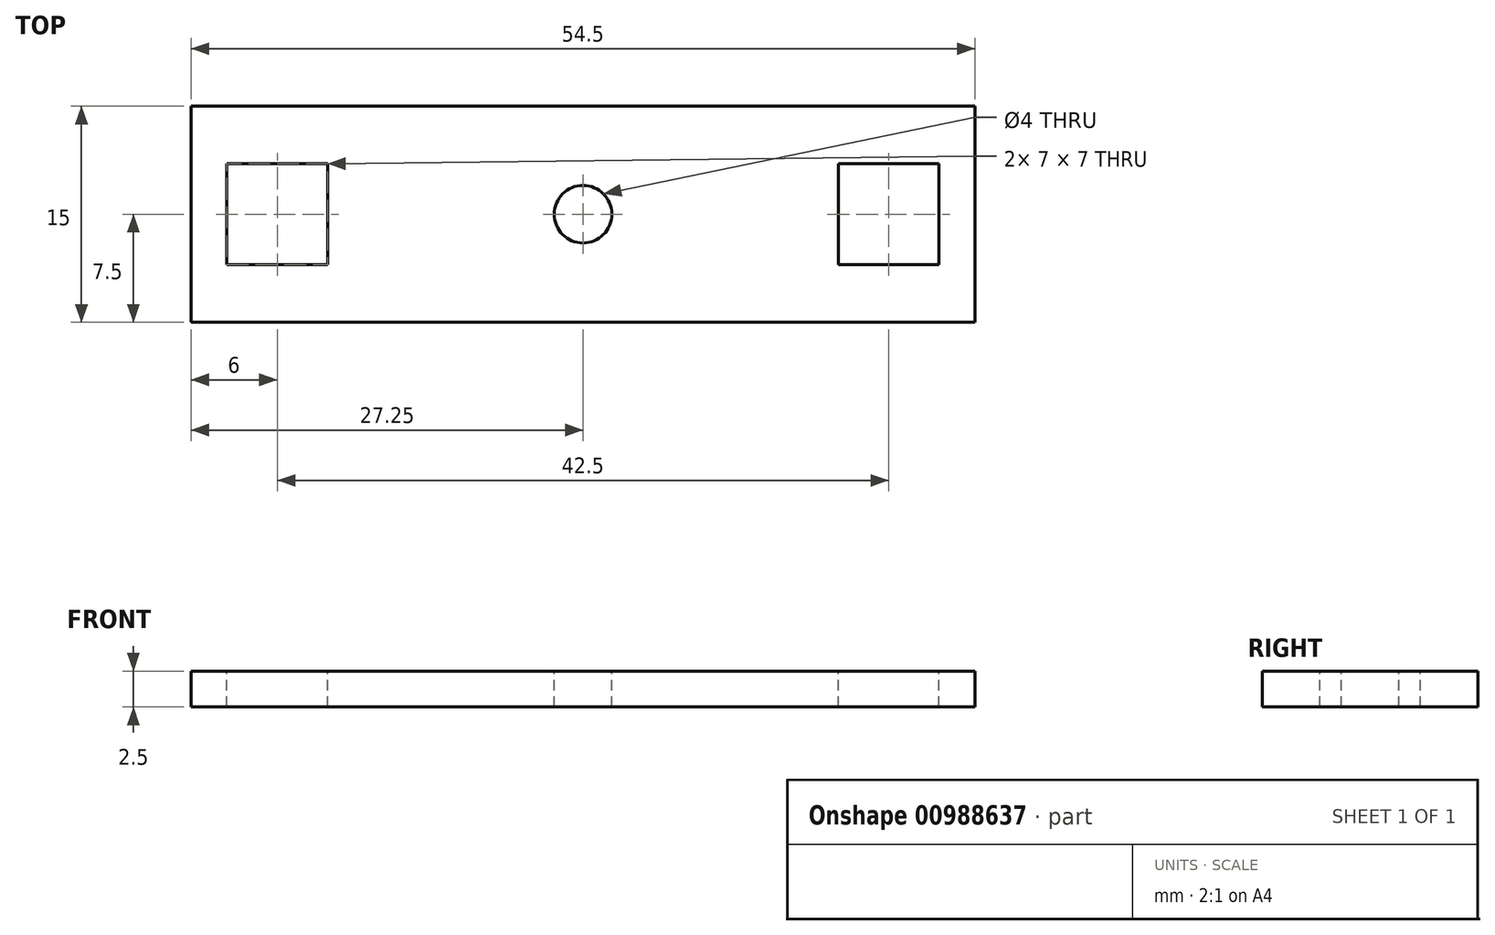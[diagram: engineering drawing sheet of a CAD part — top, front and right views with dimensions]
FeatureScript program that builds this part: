
annotation { "Feature Type Name" : "Feature", "Feature Type Description" : "" }
export const myFeature = defineFeature(function(context is Context, id is Id, definition is map)
    precondition{}
    {
        {
            var Q0;
            Q0=qCreatedBy(makeId("Top.planeOp"),FACE);
            var sketch = newSketch(context, id + "F0", { "sketchPlane" : qUnion([Q0])});
            skLineSegment(sketch, "E0.bottom", {"start": v(27.25, 7.5) * mm, "end": v(-27.25, 7.5) * mm});
            skLineSegment(sketch, "E0.top", {"start": v(27.25, -7.5) * mm, "end": v(-27.25, -7.5) * mm});
            skLineSegment(sketch, "E0.left", {"start": v(27.25, 7.5) * mm, "end": v(27.25, -7.5) * mm});
            skLineSegment(sketch, "E0.right", {"start": v(-27.25, 7.5) * mm, "end": v(-27.25, -7.5) * mm});
            skPoint(sketch, "E0.middle", {"position": v(0, 0) * mm});
            skSolve(sketch);
        }
        {
            var Q0;
            Q0=makeQuery(id+"F0.imprint","IMPRINT",FACE,{"disambiguationData":[TD([[makeQuery(id+"F0.imprint","IMPRINT",EDGE,{"derivedFrom":sQuery(id+"F0.wireOp",EDGE,"E0.bottom")}),1.0]])]});
            extrude(context, id + "F1", {"entities" : qUnion([Q0]), "depth" : 2.5 * mm, "offsetDistance" : 25 * mm});
        }
        {
            var Q0;
            Q0=makeQuery(id+"F1.opExtrude","CAP_FACE",FACE,{"disambiguationData":[OSD([sQuery(id+"F0.wireOp",EDGE,"E0.bottom"),sQuery(id+"F0.wireOp",EDGE,"E0.top"),sQuery(id+"F0.wireOp",EDGE,"E0.left"),sQuery(id+"F0.wireOp",EDGE,"E0.right")])],"isStart":false});
            var sketch = newSketch(context, id + "F2", { "sketchPlane" : qUnion([Q0])});
            skPoint(sketch, "E1", {"position": v(0, 0) * mm});
            skSolve(sketch);
        }
        {
            var Q0;
            Q0=sQuery(id+"F2.wireOp",VERTEX,"E1");
            var Q1;
            Q1=makeQuery(id+"F1.opExtrude","SWEPT_BODY",BODY,{"disambiguationData":[OSD([sQuery(id+"F0.wireOp",EDGE,"E0.bottom"),sQuery(id+"F0.wireOp",EDGE,"E0.top"),sQuery(id+"F0.wireOp",EDGE,"E0.left"),sQuery(id+"F0.wireOp",EDGE,"E0.right")])]});
            hole(context, id + "F3", {"style" : HoleStyle.SIMPLE, "endStyle" : HoleEndStyle.THROUGH, "holeDiameter" : 4 * mm, "majorDiameter" : 5 * mm, "isTappedThrough" : true, "tappedDepth" : 12 * mm, "tapClearance" : 3, "locations" : qUnion([Q0]), "scope" : qUnion([Q1])});
        }
        {
            var Q0;
            Q0=makeQuery(id+"F1.opExtrude","CAP_FACE",FACE,{"disambiguationData":[OSD([sQuery(id+"F0.wireOp",EDGE,"E0.bottom"),sQuery(id+"F0.wireOp",EDGE,"E0.top"),sQuery(id+"F0.wireOp",EDGE,"E0.left"),sQuery(id+"F0.wireOp",EDGE,"E0.right")])],"isStart":false});
            var sketch = newSketch(context, id + "F4", { "sketchPlane" : qUnion([Q0])});
            skLineSegment(sketch, "E2", {"start": v(-27.25, 0) * mm, "end": v(27.25, 0) * mm, "construction": true});
            skLineSegment(sketch, "E3", {"start": v(0, 7.5) * mm, "end": v(0, -7.5) * mm, "construction": true});
            skLineSegment(sketch, "E4", {"start": v(-21.25, 7.5) * mm, "end": v(-21.25, -7.5) * mm, "construction": true});
            skLineSegment(sketch, "E5.bottom", {"start": v(-17.75, -3.5) * mm, "end": v(-24.75, -3.5) * mm});
            skLineSegment(sketch, "E5.top", {"start": v(-17.75, 3.5) * mm, "end": v(-24.75, 3.5) * mm});
            skLineSegment(sketch, "E5.left", {"start": v(-17.75, -3.5) * mm, "end": v(-17.75, 3.5) * mm});
            skLineSegment(sketch, "E5.right", {"start": v(-24.75, -3.5) * mm, "end": v(-24.75, 3.5) * mm});
            skPoint(sketch, "E5.middle", {"position": v(-21.25, 0) * mm});
            skLineSegment(sketch, "E6.MirrorCS", {"start": v(17.75, 3.5) * mm, "end": v(24.75, 3.5) * mm});
            skLineSegment(sketch, "E7.MirrorCS", {"start": v(24.75, -3.5) * mm, "end": v(24.75, 3.5) * mm});
            skLineSegment(sketch, "E8.MirrorCS", {"start": v(17.75, -3.5) * mm, "end": v(24.75, -3.5) * mm});
            skLineSegment(sketch, "E9.MirrorCS", {"start": v(17.75, -3.5) * mm, "end": v(17.75, 3.5) * mm});
            skSolve(sketch);
        }
        {
            var Q0;
            Q0=makeQuery(id+"F4.imprint","IMPRINT",FACE,{"disambiguationData":[TD([[makeQuery(id+"F4.imprint","IMPRINT",EDGE,{"derivedFrom":sQuery(id+"F4.wireOp",EDGE,"E5.bottom")}),-1.0]])]});
            var Q1;
            Q1=makeQuery(id+"F4.imprint","IMPRINT",FACE,{"disambiguationData":[TD([[makeQuery(id+"F4.imprint","IMPRINT",EDGE,{"derivedFrom":sQuery(id+"F4.wireOp",EDGE,"E6.MirrorCS")}),-1.0]])]});
            extrude(context, id + "F5", {"entities" : qUnion([Q0, Q1]), "operationType" : NewBodyOperationType.REMOVE, "endBound" : BoundingType.THROUGH_ALL, "oppositeDirection" : true, "depth" : 25 * mm, "offsetDistance" : 25 * mm});
        }
    });
